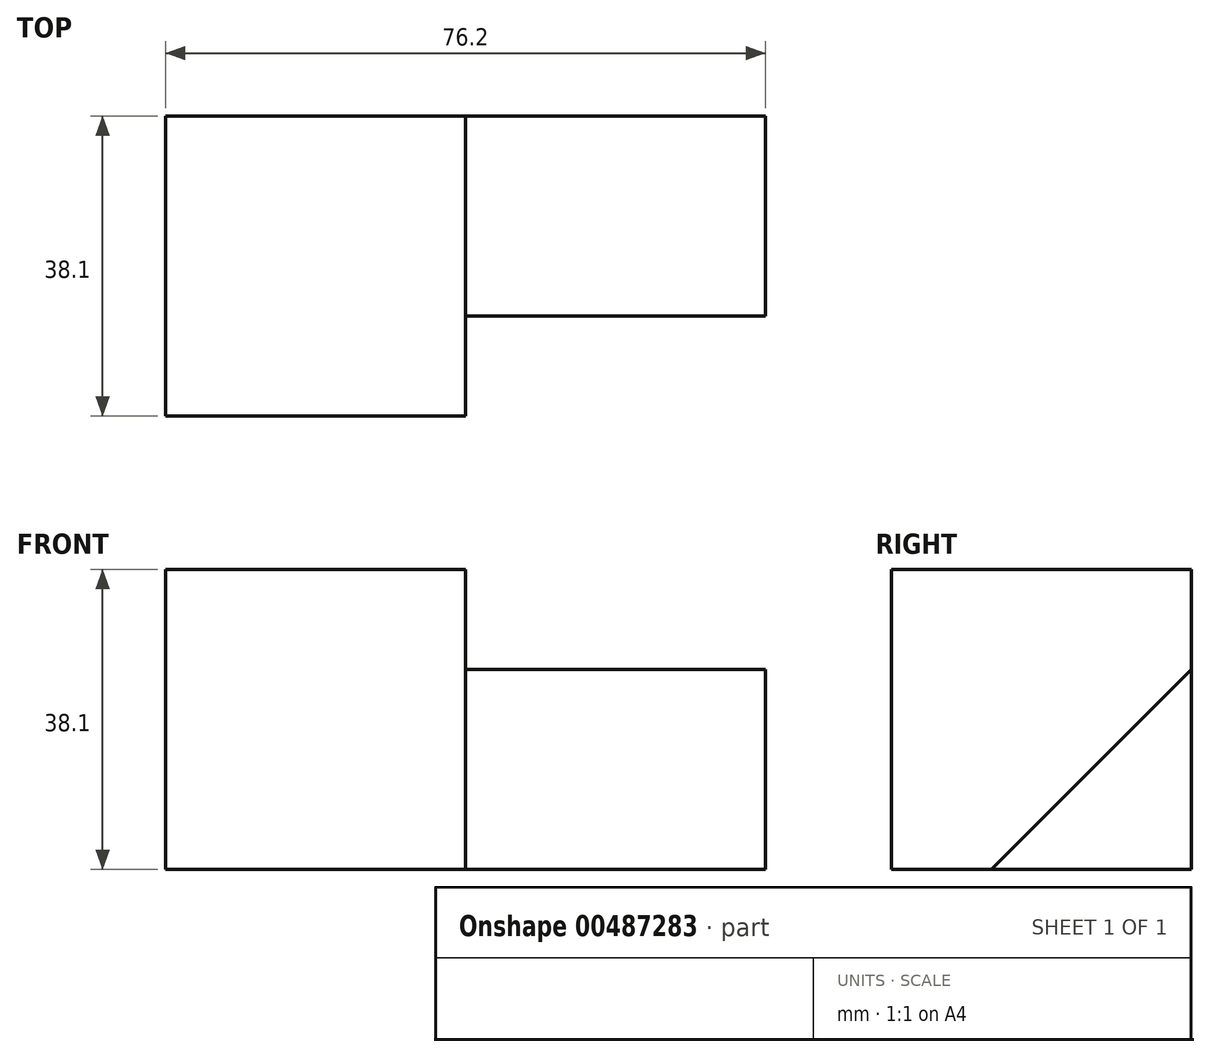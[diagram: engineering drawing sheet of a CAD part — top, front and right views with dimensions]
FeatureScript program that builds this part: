
annotation { "Feature Type Name" : "Feature", "Feature Type Description" : "" }
export const myFeature = defineFeature(function(context is Context, id is Id, definition is map)
    precondition{}
    {
        {
            var Q0;
            Q0=qCreatedBy(makeId("Top.planeOp"),FACE);
            var sketch = newSketch(context, id + "F0", { "sketchPlane" : qUnion([Q0])});
            skLineSegment(sketch, "E0", {"start": v(-16.25, -26.99) * mm, "end": v(21.85, -26.99) * mm});
            skLineSegment(sketch, "E1", {"start": v(21.85, -26.99) * mm, "end": v(21.85, 11.11) * mm});
            skLineSegment(sketch, "E2", {"start": v(21.85, 11.11) * mm, "end": v(-16.25, 11.11) * mm});
            skLineSegment(sketch, "E3", {"start": v(-16.25, 11.11) * mm, "end": v(-16.25, -26.99) * mm});
            skSolve(sketch);
        }
        {
            var Q0;
            Q0=makeQuery(id+"F0.imprint","IMPRINT",FACE,{"disambiguationData":[TD([[makeQuery(id+"F0.imprint","IMPRINT",EDGE,{"derivedFrom":sQuery(id+"F0.wireOp",EDGE,"E0")}),1.0]])]});
            extrude(context, id + "F1", {"entities" : qUnion([Q0]), "depth" : 38.1 * mm});
        }
        {
            var Q0;
            Q0=makeQuery(id+"F1.opExtrude","SWEPT_FACE",FACE,{"disambiguationData":[OSD([sQuery(id+"F0.wireOp",EDGE,"E1")])]});
            var sketch = newSketch(context, id + "F2", { "sketchPlane" : qUnion([Q0])});
            skLineSegment(sketch, "E4", {"start": v(11.11, 25.4) * mm, "end": v(-14.29, 0) * mm});
            skLineSegment(sketch, "E5", {"start": v(-14.29, 0) * mm, "end": v(11.11, 0) * mm});
            skLineSegment(sketch, "E6", {"start": v(11.11, 0) * mm, "end": v(11.11, 25.4) * mm});
            skSolve(sketch);
        }
        {
            var Q0;
            Q0=makeQuery(id+"F2.imprint","IMPRINT",FACE,{"disambiguationData":[TD([[makeQuery(id+"F2.imprint","IMPRINT",EDGE,{"derivedFrom":sQuery(id+"F2.wireOp",EDGE,"E4")}),1.0]])]});
            extrude(context, id + "F3", {"entities" : qUnion([Q0]), "operationType" : NewBodyOperationType.ADD, "depth" : 38.1 * mm});
        }
    });
